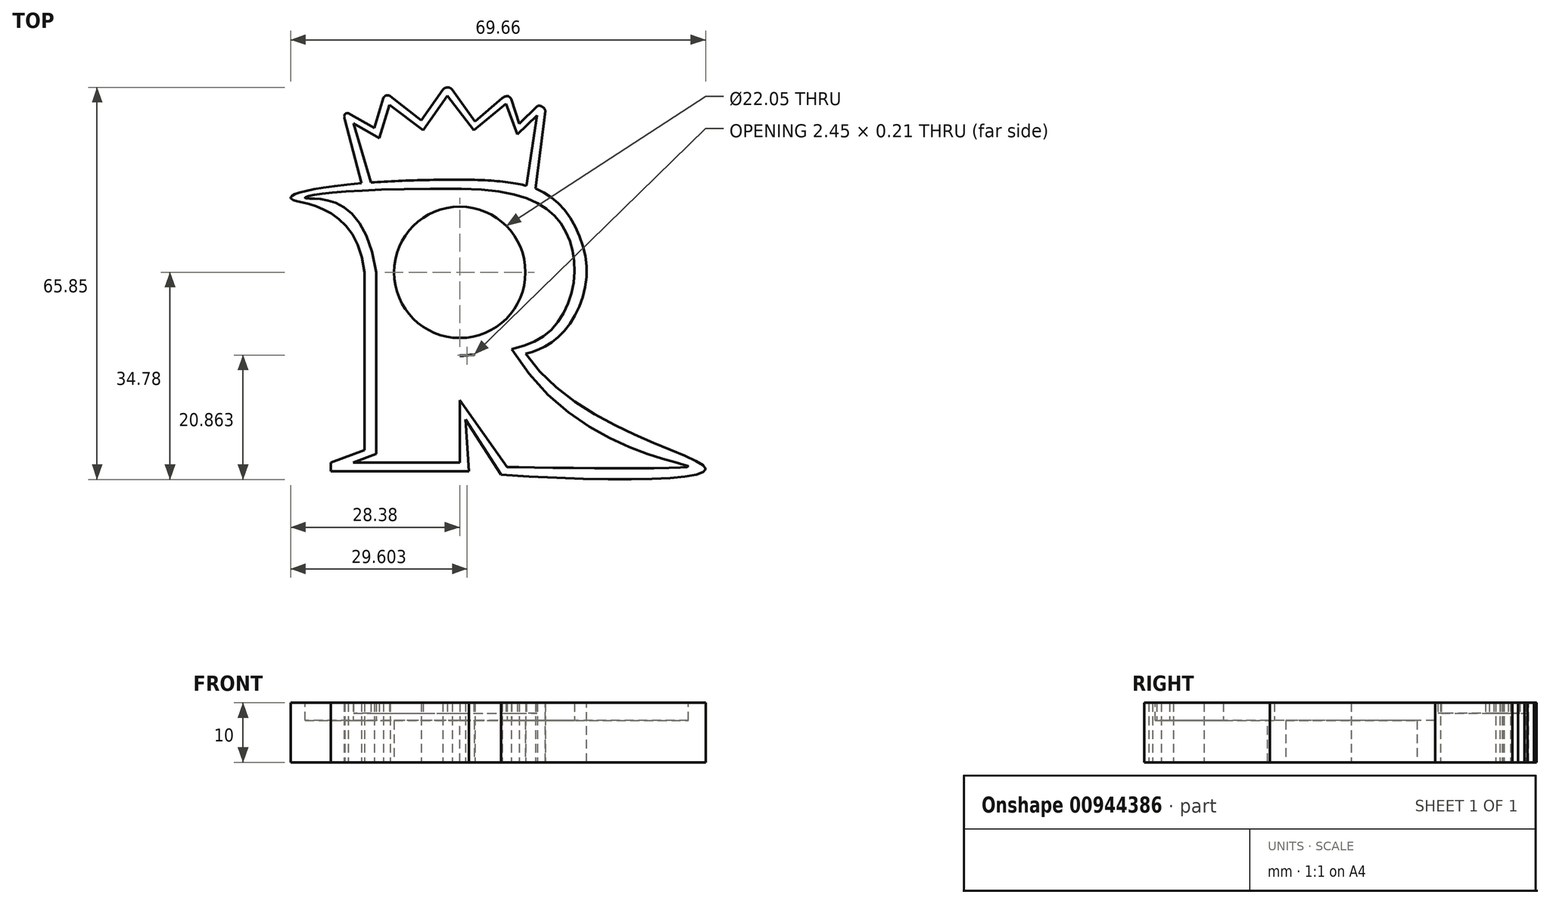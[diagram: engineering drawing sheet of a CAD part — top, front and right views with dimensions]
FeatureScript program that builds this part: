
annotation { "Feature Type Name" : "Feature", "Feature Type Description" : "" }
export const myFeature = defineFeature(function(context is Context, id is Id, definition is map)
    precondition{}
    {
        {
            var Q0;
            Q0=qCreatedBy(makeId("Top.planeOp"),FACE);
            var sketch = newSketch(context, id + "F0", { "sketchPlane" : qUnion([Q0])});
            skCircle(sketch, "E0", {"center": v(0, 0) * mm, "radius": 11.03 * mm});
            skCircle(sketch, "E1", {"center": v(0, 0) * mm, "radius": 14.03 * mm});
            skLineSegment(sketch, "E2", {"start": v(-14.03, 0) * mm, "end": v(-14.03, -30.49) * mm});
            skLineSegment(sketch, "E3", {"start": v(-14.03, -30.49) * mm, "end": v(-17.91, -31.92) * mm});
            skLineSegment(sketch, "E4", {"start": v(-17.91, -31.92) * mm, "end": v(0, -31.92) * mm});
            skLineSegment(sketch, "E5", {"start": v(0, -31.92) * mm, "end": v(0, -21.47) * mm});
            skLineSegment(sketch, "E6", {"start": v(0, -21.47) * mm, "end": v(7.94, -32.68) * mm});
            skFitSpline(sketch, "E7", {"points": [v(7.94, -32.68) * mm, v(38.2, -32.68) * mm, v(7.94, -11.56) * mm], "startDerivative": vector(37.47, -0.84) * mm, "endDerivative": vector(-59.98, 109.36) * mm});
            skFitSpline(sketch, "E8", {"points": [v(0, 14.03) * mm, v(-25.42, 12.4) * mm, v(-14.03, 0) * mm], "startDerivative": vector(-121.25, 0.7) * mm, "endDerivative": vector(12.5, -87.68) * mm});
            skFitSpline(sketch, "E9", {"points": [v(0, 14.03) * mm, v(16.41, 8.9) * mm, v(19.25, 0) * mm, v(15.47, -9.55) * mm, v(0, -14.03) * mm], "startDerivative": vector(95.47, -0.8) * mm, "endDerivative": vector(-85.74, -6.84) * mm});
            skLineSegment(sketch, "E10", {"start": v(-16.02, 0) * mm, "end": v(-16.02, -29.84) * mm});
            skLineSegment(sketch, "E11", {"start": v(-16.02, -29.84) * mm, "end": v(-21.66, -31.92) * mm});
            skLineSegment(sketch, "E12", {"start": v(-21.66, -31.92) * mm, "end": v(-21.66, -33.38) * mm});
            skLineSegment(sketch, "E13", {"start": v(-21.66, -33.38) * mm, "end": v(1.55, -33.38) * mm});
            skLineSegment(sketch, "E14", {"start": v(1.55, -33.38) * mm, "end": v(0.96, -24.73) * mm});
            skLineSegment(sketch, "E15", {"start": v(0.96, -24.73) * mm, "end": v(6.93, -33.97) * mm});
            skFitSpline(sketch, "E16", {"points": [v(6.93, -33.97) * mm, v(41.22, -32.8) * mm, v(11.06, -13.65) * mm], "startDerivative": vector(108.61, -7.96) * mm, "endDerivative": vector(-48.24, 73.14) * mm});
            skFitSpline(sketch, "E17", {"points": [v(0, 15.56) * mm, v(16.85, 11.27) * mm, v(21.3, 0) * mm, v(16.9, -10.51) * mm, v(11.06, -13.65) * mm], "startDerivative": vector(95.47, -0.8) * mm, "endDerivative": vector(-28.72, -5.97) * mm});
            skFitSpline(sketch, "E18", {"points": [v(-16.02, 0) * mm, v(-28.1, 12.22) * mm, v(0, 15.56) * mm], "startDerivative": vector(-7.34, 77.03) * mm, "endDerivative": vector(106.56, 0.03) * mm});
            skLineSegment(sketch, "E19", {"start": v(-14.9, 15.07) * mm, "end": v(-17.82, 24.98) * mm});
            skLineSegment(sketch, "E20", {"start": v(-17.82, 24.98) * mm, "end": v(-13.49, 22.5) * mm});
            skLineSegment(sketch, "E21", {"start": v(-13.49, 22.5) * mm, "end": v(-11.78, 28.13) * mm});
            skLineSegment(sketch, "E22", {"start": v(-11.78, 28.13) * mm, "end": v(-6.16, 23.9) * mm});
            skLineSegment(sketch, "E23", {"start": v(-6.16, 23.9) * mm, "end": v(-2.1, 29.62) * mm});
            skLineSegment(sketch, "E24", {"start": v(-2.1, 29.62) * mm, "end": v(2.37, 23.9) * mm});
            skLineSegment(sketch, "E25", {"start": v(2.37, 23.9) * mm, "end": v(7.8, 28.3) * mm});
            skLineSegment(sketch, "E26", {"start": v(7.8, 28.3) * mm, "end": v(9.7, 23.15) * mm});
            skLineSegment(sketch, "E27", {"start": v(9.7, 23.15) * mm, "end": v(13, 26.35) * mm});
            skLineSegment(sketch, "E28", {"start": v(13, 26.35) * mm, "end": v(11.2, 14.54) * mm});
            skLineSegment(sketch, "E29", {"start": v(-16.5, 14.95) * mm, "end": v(-19.3, 25.62) * mm});
            skLineSegment(sketch, "E30", {"start": v(-18.72, 26.72) * mm, "end": v(-14.34, 24.24) * mm});
            skLineSegment(sketch, "E31", {"start": v(-14.34, 24.24) * mm, "end": v(-12.8, 29.31) * mm});
            skLineSegment(sketch, "E32", {"start": v(-11.7, 29.59) * mm, "end": v(-6.45, 25.54) * mm});
            skLineSegment(sketch, "E33", {"start": v(-6.45, 25.54) * mm, "end": v(-2.84, 30.63) * mm});
            skLineSegment(sketch, "E34", {"start": v(-1.24, 30.63) * mm, "end": v(2.56, 25.31) * mm});
            skLineSegment(sketch, "E35", {"start": v(2.56, 25.31) * mm, "end": v(7.14, 29.26) * mm});
            skLineSegment(sketch, "E36", {"start": v(8.68, 29.06) * mm, "end": v(10, 24.96) * mm});
            skLineSegment(sketch, "E37", {"start": v(10, 24.96) * mm, "end": v(13.01, 27.91) * mm});
            skLineSegment(sketch, "E38", {"start": v(14.35, 27.02) * mm, "end": v(12.7, 14.06) * mm});
            skFitSpline(sketch, "E39", {"points": [v(13.01, 27.91) * mm, v(14.35, 27.02) * mm], "startDerivative": vector(1.66, 0.7) * mm, "endDerivative": vector(-0.03, -1.81) * mm});
            skFitSpline(sketch, "E40", {"points": [v(8.68, 29.06) * mm, v(7.14, 29.26) * mm], "startDerivative": vector(-1.2, 2.05) * mm, "endDerivative": vector(-2.04, -1.39) * mm});
            skFitSpline(sketch, "E41", {"points": [v(-2.84, 30.63) * mm, v(-1.24, 30.63) * mm], "startDerivative": vector(1.45, 1.73) * mm, "endDerivative": vector(1.34, -1.77) * mm});
            skFitSpline(sketch, "E42", {"points": [v(-12.8, 29.31) * mm, v(-11.7, 29.59) * mm], "startDerivative": vector(0.52, 1.26) * mm, "endDerivative": vector(1.43, -0.87) * mm});
            skFitSpline(sketch, "E43", {"points": [v(-18.72, 26.72) * mm, v(-19.3, 25.62) * mm], "startDerivative": vector(-2.15, 0.24) * mm, "endDerivative": vector(0.53, -1.88) * mm});
            skSolve(sketch);
        }
        {
            var Q0;
            {var subQ3=sQuery(id+"F0.wireOp",EDGE,"E19");Q0=makeQuery(id+"F0.imprint","IMPRINT",FACE,{"disambiguationData":[TD([[makeQuery(id+"F0.imprint","IMPRINT",EDGE,{"derivedFrom":subQ3}),1.0]])]});}
            var Q1;
            Q1=makeQuery(id+"F0.imprint","IMPRINT",FACE,{"disambiguationData":[TD([[makeQuery(id+"F0.imprint","IMPRINT",EDGE,{"derivedFrom":sQuery(id+"F0.wireOp",EDGE,"E2")}),-1.0]])]});
            extrude(context, id + "F1", {"entities" : qUnion([Q0, Q1]), "depth" : 10 * mm, "offsetDistance" : 25 * mm});
        }
        {
            var Q0;
            {var subQ0=sQuery(id+"F0.wireOp",EDGE,"E7");var subQ1=sQuery(id+"F0.wireOp",EDGE,"E1");var subQ2=makeQuery(id+"F0.imprint","INTERSECT",VERTEX,{"derivedFrom":[subQ1,subQ0]});Q0=makeQuery(id+"F0.imprint","IMPRINT",FACE,{"disambiguationData":[TD([[makeQuery(id+"F0.imprint","IMPRINT",EDGE,{"disambiguationData":[TD([[subQ2,-1.0]])],"derivedFrom":subQ1}),-1.0]])]});}
            var Q1;
            {var subQ0=sQuery(id+"F0.wireOp",EDGE,"E8");Q1=makeQuery(id+"F0.imprint","IMPRINT",FACE,{"disambiguationData":[TD([[makeQuery(id+"F0.imprint","IMPRINT",EDGE,{"derivedFrom":subQ0}),1.0]])]});}
            var Q2;
            {var subQ0=sQuery(id+"F0.wireOp",EDGE,"E2");Q2=makeQuery(id+"F0.imprint","IMPRINT",FACE,{"disambiguationData":[TD([[makeQuery(id+"F0.imprint","IMPRINT",EDGE,{"derivedFrom":subQ0}),1.0]])]});}
            var Q3;
            {var subQ0=sQuery(id+"F0.wireOp",EDGE,"E7");var subQ1=sQuery(id+"F0.wireOp",EDGE,"E1");var subQ2=makeQuery(id+"F0.imprint","INTERSECT",VERTEX,{"derivedFrom":[subQ1,subQ0]});Q3=makeQuery(id+"F0.imprint","IMPRINT",FACE,{"disambiguationData":[TD([[makeQuery(id+"F0.imprint","IMPRINT",EDGE,{"disambiguationData":[TD([[subQ2,1.0]])],"derivedFrom":subQ1}),-1.0]])]});}
            var Q4;
            Q4=makeQuery(id+"F0.imprint","IMPRINT",FACE,{"disambiguationData":[TD([[makeQuery(id+"F0.imprint","IMPRINT",EDGE,{"derivedFrom":sQuery(id+"F0.wireOp",EDGE,"E0")}),-1.0]])]});
            extrude(context, id + "F2", {"entities" : qUnion([Q0, Q1, Q2, Q3, Q4]), "operationType" : NewBodyOperationType.ADD, "depth" : 7 * mm, "offsetDistance" : 25 * mm});
        }
        {
            var Q0;
            {var subQ4=sQuery(id+"F0.wireOp",EDGE,"E19");Q0=makeQuery(id+"F0.imprint","IMPRINT",FACE,{"disambiguationData":[TD([[makeQuery(id+"F0.imprint","IMPRINT",EDGE,{"derivedFrom":subQ4}),-1.0]])]});}
            extrude(context, id + "F3", {"entities" : qUnion([Q0]), "operationType" : NewBodyOperationType.ADD, "depth" : 8.2 * mm, "offsetDistance" : 25 * mm});
        }
    });
